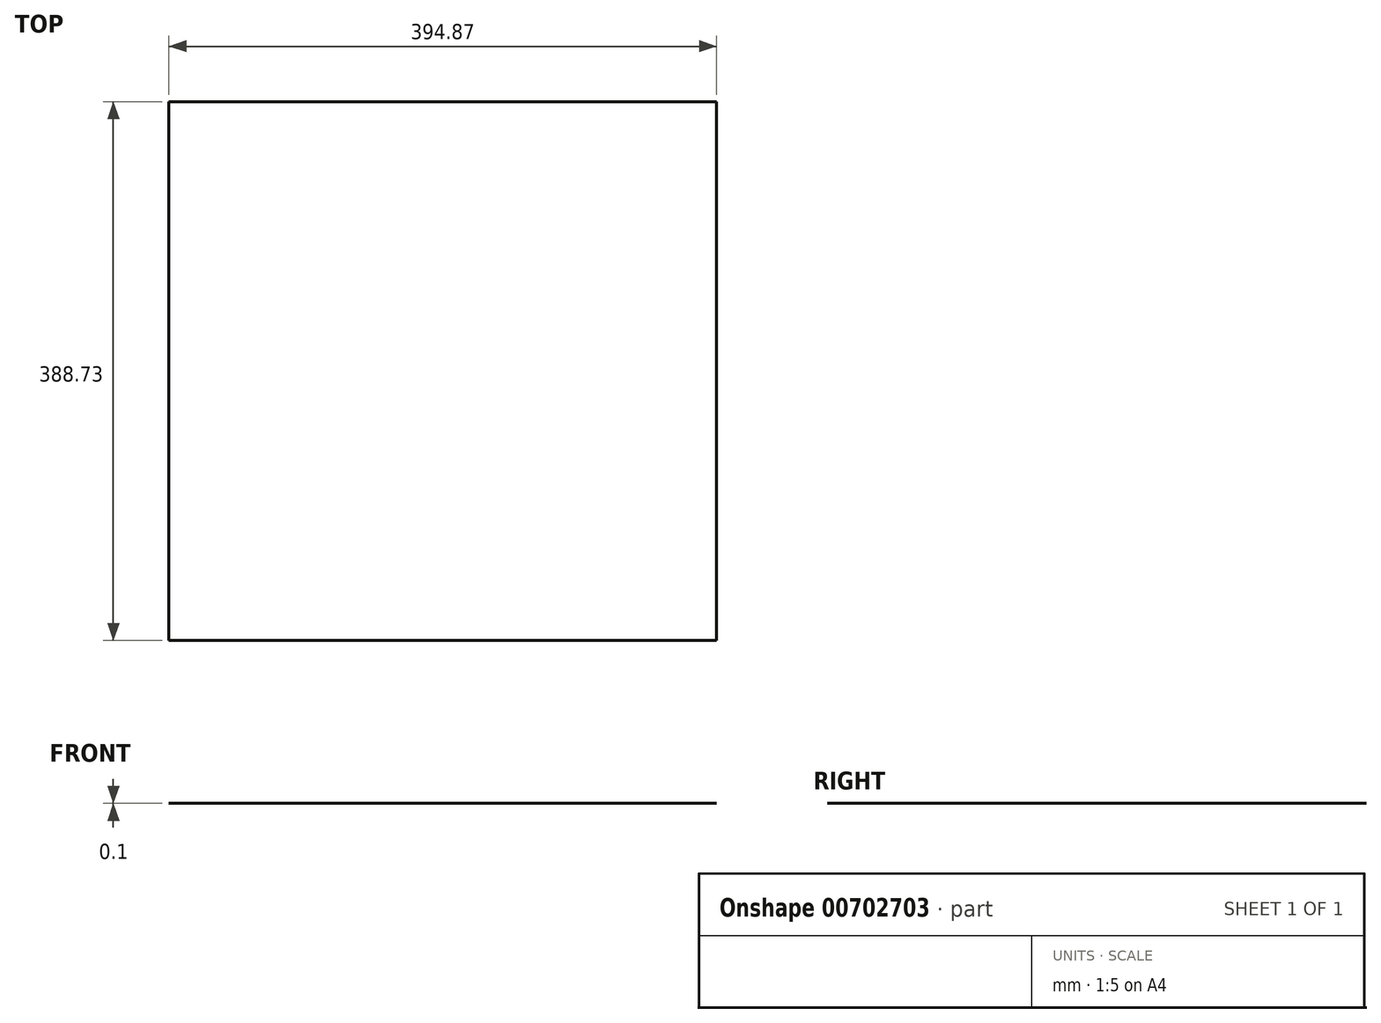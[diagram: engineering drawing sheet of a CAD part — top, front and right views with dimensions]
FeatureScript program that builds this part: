
annotation { "Feature Type Name" : "Feature", "Feature Type Description" : "" }
export const myFeature = defineFeature(function(context is Context, id is Id, definition is map)
    precondition{}
    {
        {
            var Q0;
            Q0=qCreatedBy(makeId("Top.planeOp"),FACE);
            var sketch = newSketch(context, id + "F0", { "sketchPlane" : qUnion([Q0])});
            skLineSegment(sketch, "E0.bottom", {"start": v(-186.9, 236.2) * mm, "end": v(207.97, 236.2) * mm});
            skLineSegment(sketch, "E0.top", {"start": v(-186.9, -152.53) * mm, "end": v(207.97, -152.53) * mm});
            skLineSegment(sketch, "E0.left", {"start": v(-186.9, 236.2) * mm, "end": v(-186.9, -152.53) * mm});
            skLineSegment(sketch, "E0.right", {"start": v(207.97, 236.2) * mm, "end": v(207.97, -152.53) * mm});
            skSolve(sketch);
        }
        {
            var Q0;
            Q0=makeQuery(id+"F0.imprint","IMPRINT",FACE,{"disambiguationData":[TD([[makeQuery(id+"F0.imprint","IMPRINT",EDGE,{"derivedFrom":sQuery(id+"F0.wireOp",EDGE,"E0.bottom")}),-1.0]])]});
            extrude(context, id + "F1", {"entities" : qUnion([Q0]), "depth" : 0.1 * mm, "offsetDistance" : 25.4 * mm});
        }
    });
